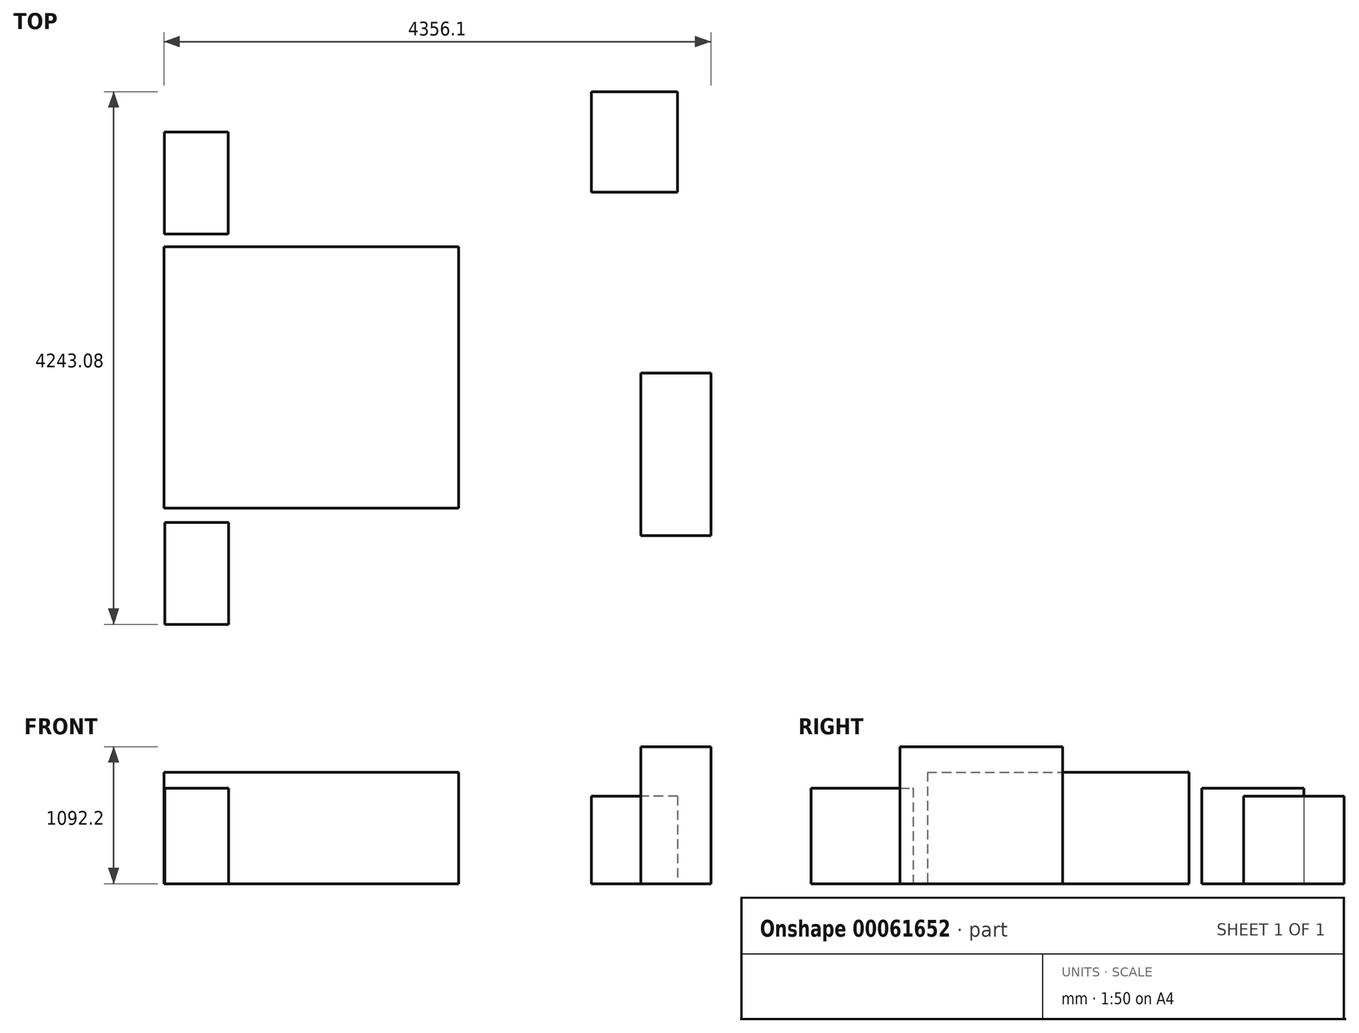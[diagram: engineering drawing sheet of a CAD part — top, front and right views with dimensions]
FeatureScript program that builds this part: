
annotation { "Feature Type Name" : "Feature", "Feature Type Description" : "" }
export const myFeature = defineFeature(function(context is Context, id is Id, definition is map)
    precondition{}
    {
        {
            var Q0;
            Q0=qCreatedBy(makeId("Top.planeOp"),FACE);
            var sketch = newSketch(context, id + "F0", { "sketchPlane" : qUnion([Q0])});
            skLineSegment(sketch, "E0.rect.bottom", {"start": v(2209.8, -2489.2) * mm, "end": v(-2209.8, -2489.2) * mm});
            skLineSegment(sketch, "E0.rect.top", {"start": v(2209.8, 2489.2) * mm, "end": v(-2209.8, 2489.2) * mm});
            skLineSegment(sketch, "E0.rect.left", {"start": v(2209.8, -2489.2) * mm, "end": v(2209.8, 2489.2) * mm});
            skLineSegment(sketch, "E0.rect.right", {"start": v(-2209.8, -2489.2) * mm, "end": v(-2209.8, 2489.2) * mm});
            skPoint(sketch, "E0.rect.middle", {"position": v(0, 0) * mm});
            skLineSegment(sketch, "E1", {"start": v(2159, -14.02) * mm, "end": v(2159, -1334.82) * mm, "construction": true});
            skLineSegment(sketch, "E2.rect.bottom", {"start": v(2178.05, -1259.86) * mm, "end": v(1619.25, -1259.86) * mm});
            skLineSegment(sketch, "E2.rect.top", {"start": v(2178.05, 35.54) * mm, "end": v(1619.25, 35.54) * mm});
            skLineSegment(sketch, "E2.rect.left", {"start": v(2178.05, -1259.86) * mm, "end": v(2178.05, 35.54) * mm});
            skLineSegment(sketch, "E2.rect.right", {"start": v(1619.25, -1259.86) * mm, "end": v(1619.25, 35.54) * mm});
            skPoint(sketch, "E2.rect.middle", {"position": v(1898.65, -612.16) * mm});
            skLineSegment(sketch, "E3.rect.bottom", {"start": v(171.45, -1041.4) * mm, "end": v(-2178.05, -1041.4) * mm});
            skLineSegment(sketch, "E3.rect.top", {"start": v(171.45, 1041.4) * mm, "end": v(-2178.05, 1041.4) * mm});
            skLineSegment(sketch, "E3.rect.left", {"start": v(171.45, -1041.4) * mm, "end": v(171.45, 1041.4) * mm});
            skLineSegment(sketch, "E3.rect.right", {"start": v(-2178.05, -1041.4) * mm, "end": v(-2178.05, 1041.4) * mm});
            skPoint(sketch, "E3.rect.middle", {"position": v(-1003.3, 0) * mm});
            skLineSegment(sketch, "E4.rect.bottom", {"start": v(1913.62, 1476.5) * mm, "end": v(1227.82, 1476.5) * mm});
            skLineSegment(sketch, "E4.rect.top", {"start": v(1913.62, 2276.6) * mm, "end": v(1227.82, 2276.6) * mm});
            skLineSegment(sketch, "E4.rect.left", {"start": v(1913.62, 1476.5) * mm, "end": v(1913.62, 2276.6) * mm});
            skLineSegment(sketch, "E4.rect.right", {"start": v(1227.82, 1476.5) * mm, "end": v(1227.82, 2276.6) * mm});
            skPoint(sketch, "E4.rect.middle", {"position": v(1570.72, 1876.54) * mm});
            skLineSegment(sketch, "E5.rect.bottom", {"start": v(-1664.65, 1142.16) * mm, "end": v(-2172.65, 1142.16) * mm});
            skLineSegment(sketch, "E5.rect.top", {"start": v(-1664.65, 1954.96) * mm, "end": v(-2172.65, 1954.96) * mm});
            skLineSegment(sketch, "E5.rect.left", {"start": v(-1664.65, 1142.16) * mm, "end": v(-1664.65, 1954.96) * mm});
            skLineSegment(sketch, "E5.rect.right", {"start": v(-2172.65, 1142.16) * mm, "end": v(-2172.65, 1954.96) * mm});
            skPoint(sketch, "E5.rect.middle", {"position": v(-1918.65, 1548.56) * mm});
            skLineSegment(sketch, "E6.rect.bottom", {"start": v(-1662.66, -1966.49) * mm, "end": v(-2170.66, -1966.49) * mm});
            skLineSegment(sketch, "E6.rect.top", {"start": v(-1662.66, -1153.69) * mm, "end": v(-2170.66, -1153.69) * mm});
            skLineSegment(sketch, "E6.rect.left", {"start": v(-1662.66, -1966.49) * mm, "end": v(-1662.66, -1153.69) * mm});
            skLineSegment(sketch, "E6.rect.right", {"start": v(-2170.66, -1966.49) * mm, "end": v(-2170.66, -1153.69) * mm});
            skPoint(sketch, "E6.rect.middle", {"position": v(-1916.66, -1560.09) * mm});
            skSolve(sketch);
        }
        {
            var Q0;
            Q0=sQuery(id+"F0.wireOp",EDGE,"E0.rect.right");
            var Q1;
            Q1=sQuery(id+"F0.wireOp",EDGE,"E0.rect.top");
            var Q2;
            Q2=sQuery(id+"F0.wireOp",EDGE,"E0.rect.bottom");
            extrude(context, id + "F1", {"bodyType" : ToolBodyType.SURFACE, "surfaceEntities" : qUnion([Q0, Q1, Q2]), "depth" : 3048 * mm});
        }
        {
            var Q0;
            Q0=makeQuery(id+"F0.imprint","IMPRINT",FACE,{"disambiguationData":[TD([[makeQuery(id+"F0.imprint","IMPRINT",EDGE,{"derivedFrom":sQuery(id+"F0.wireOp",EDGE,"E6.rect.bottom")}),-1.0]])]});
            var Q1;
            Q1=makeQuery(id+"F0.imprint","IMPRINT",FACE,{"disambiguationData":[TD([[makeQuery(id+"F0.imprint","IMPRINT",EDGE,{"derivedFrom":sQuery(id+"F0.wireOp",EDGE,"E5.rect.bottom")}),-1.0]])]});
            extrude(context, id + "F2", {"entities" : qUnion([Q0, Q1]), "depth" : 762 * mm});
        }
        {
            var Q0;
            Q0=makeQuery(id+"F0.imprint","IMPRINT",FACE,{"disambiguationData":[TD([[makeQuery(id+"F0.imprint","IMPRINT",EDGE,{"derivedFrom":sQuery(id+"F0.wireOp",EDGE,"E3.rect.bottom")}),-1.0]])]});
            extrude(context, id + "F3", {"entities" : qUnion([Q0]), "depth" : 889 * mm});
        }
        {
            var Q0;
            Q0=sQuery(id+"F0.wireOp",EDGE,"E3.rect.right");
            extrude(context, id + "F4", {"bodyType" : ToolBodyType.SURFACE, "surfaceEntities" : qUnion([Q0]), "depth" : 1638.3 * mm});
        }
        {
            var Q0;
            Q0=makeQuery(id+"F0.imprint","IMPRINT",FACE,{"disambiguationData":[TD([[makeQuery(id+"F0.imprint","IMPRINT",EDGE,{"derivedFrom":sQuery(id+"F0.wireOp",EDGE,"E2.rect.bottom")}),-1.0]])]});
            extrude(context, id + "F5", {"entities" : qUnion([Q0]), "depth" : 1092.2 * mm});
        }
        {
            var Q0;
            Q0=makeQuery(id+"F0.imprint","IMPRINT",FACE,{"disambiguationData":[TD([[makeQuery(id+"F0.imprint","IMPRINT",EDGE,{"derivedFrom":sQuery(id+"F0.wireOp",EDGE,"E4.rect.bottom")}),-1.0]])]});
            extrude(context, id + "F6", {"entities" : qUnion([Q0]), "depth" : 698.5 * mm});
        }
    });
